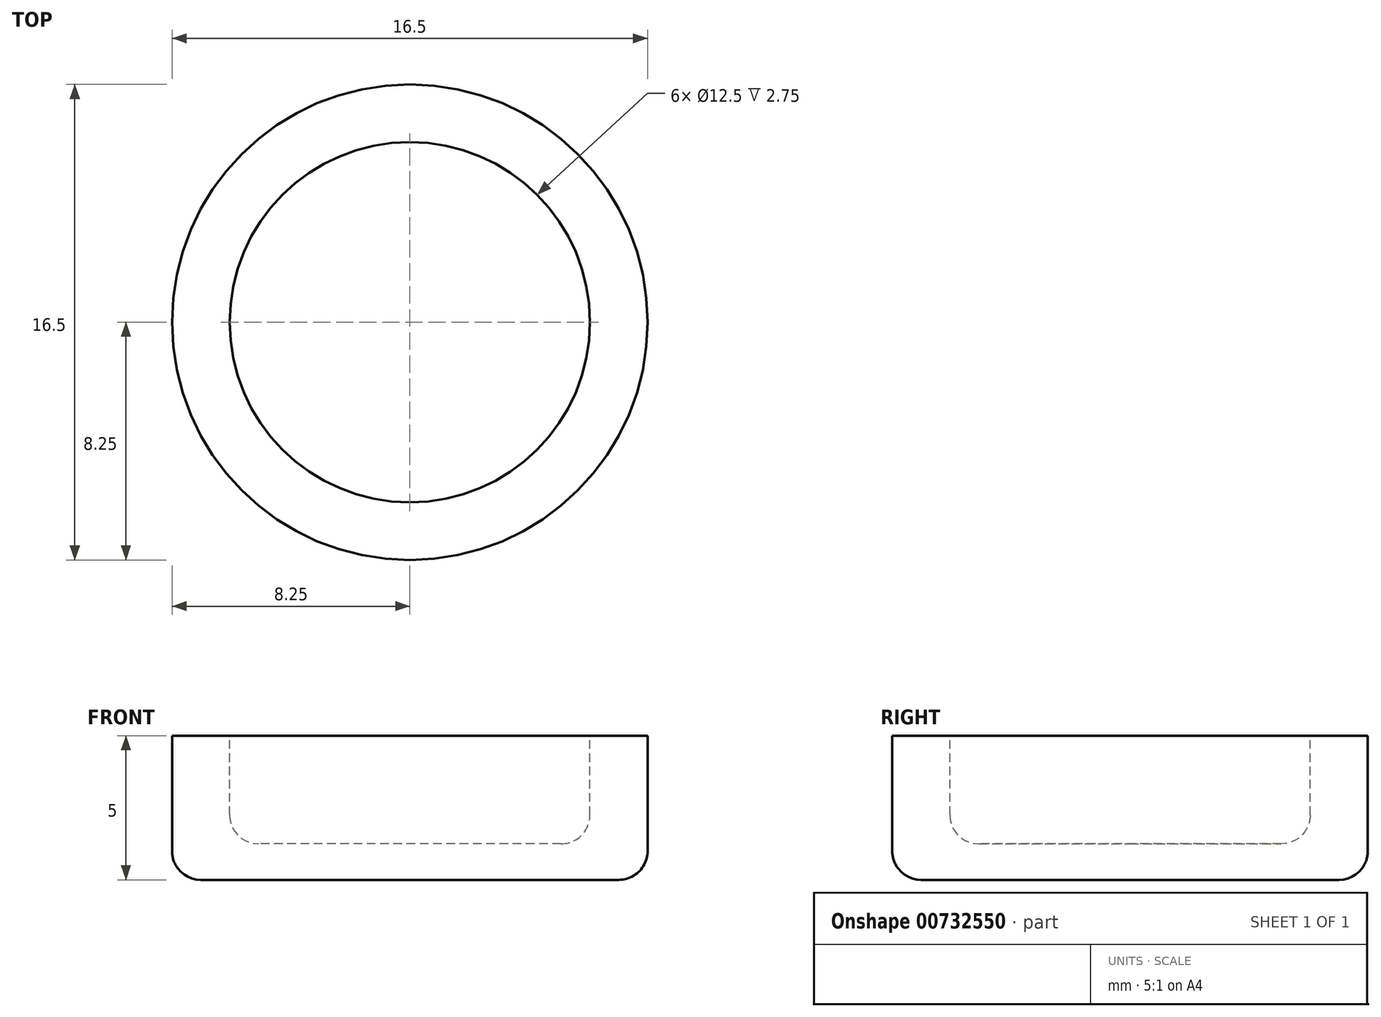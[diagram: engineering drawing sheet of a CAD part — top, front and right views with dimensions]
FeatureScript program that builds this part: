
annotation { "Feature Type Name" : "Feature", "Feature Type Description" : "" }
export const myFeature = defineFeature(function(context is Context, id is Id, definition is map)
    precondition{}
    {
        {
            var Q0;
            Q0=qCreatedBy(makeId("Top.planeOp"),FACE);
            var sketch = newSketch(context, id + "F0", { "sketchPlane" : qUnion([Q0])});
            skCircle(sketch, "E0", {"center": v(0, 0) * mm, "radius": 8.25 * mm});
            skSolve(sketch);
        }
        {
            var Q0;
            Q0 = qSketchRegion(id + "F0", true);
            extrude(context, id + "F1", {"entities" : qUnion([Q0]), "depth" : 5 * mm, "offsetDistance" : 25 * mm});
        }
        {
            var Q0;
            Q0=makeQuery(id+"F1.opExtrude","CAP_FACE",FACE,{"disambiguationData":[OSD([sQuery(id+"F0.wireOp",EDGE,"E0")])],"isStart":false});
            var sketch = newSketch(context, id + "F2", { "sketchPlane" : qUnion([Q0])});
            skCircle(sketch, "E1", {"center": v(0, 0) * mm, "radius": 6.25 * mm});
            skSolve(sketch);
        }
        {
            var Q0;
            Q0 = qSketchRegion(id + "F2", true);
            extrude(context, id + "F3", {"entities" : qUnion([Q0]), "operationType" : NewBodyOperationType.REMOVE, "oppositeDirection" : true, "depth" : 3.75 * mm, "offsetDistance" : 25 * mm});
        }
        {
            var Q0;
            Q0=makeQuery(id+"F1.opExtrude","CAP_EDGE",EDGE,{"disambiguationData":[OSD([sQuery(id+"F0.wireOp",EDGE,"E0")])],"isStart":true});
            var Q1;
            Q1=makeQuery(id+"F3.boolean.opBoolean","COPY",EDGE,{"derivedFrom":makeQuery(id+"F3.opExtrude","CAP_EDGE",EDGE,{"disambiguationData":[OSD([sQuery(id+"F2.wireOp",EDGE,"E1")])],"isStart":false})});
            fillet(context, id + "F4", {"entities" : qUnion([Q0, Q1]), "radius" : 1 * mm, "tangentPropagation" : true, "allowEdgeOverflow" : false});
        }
    });
